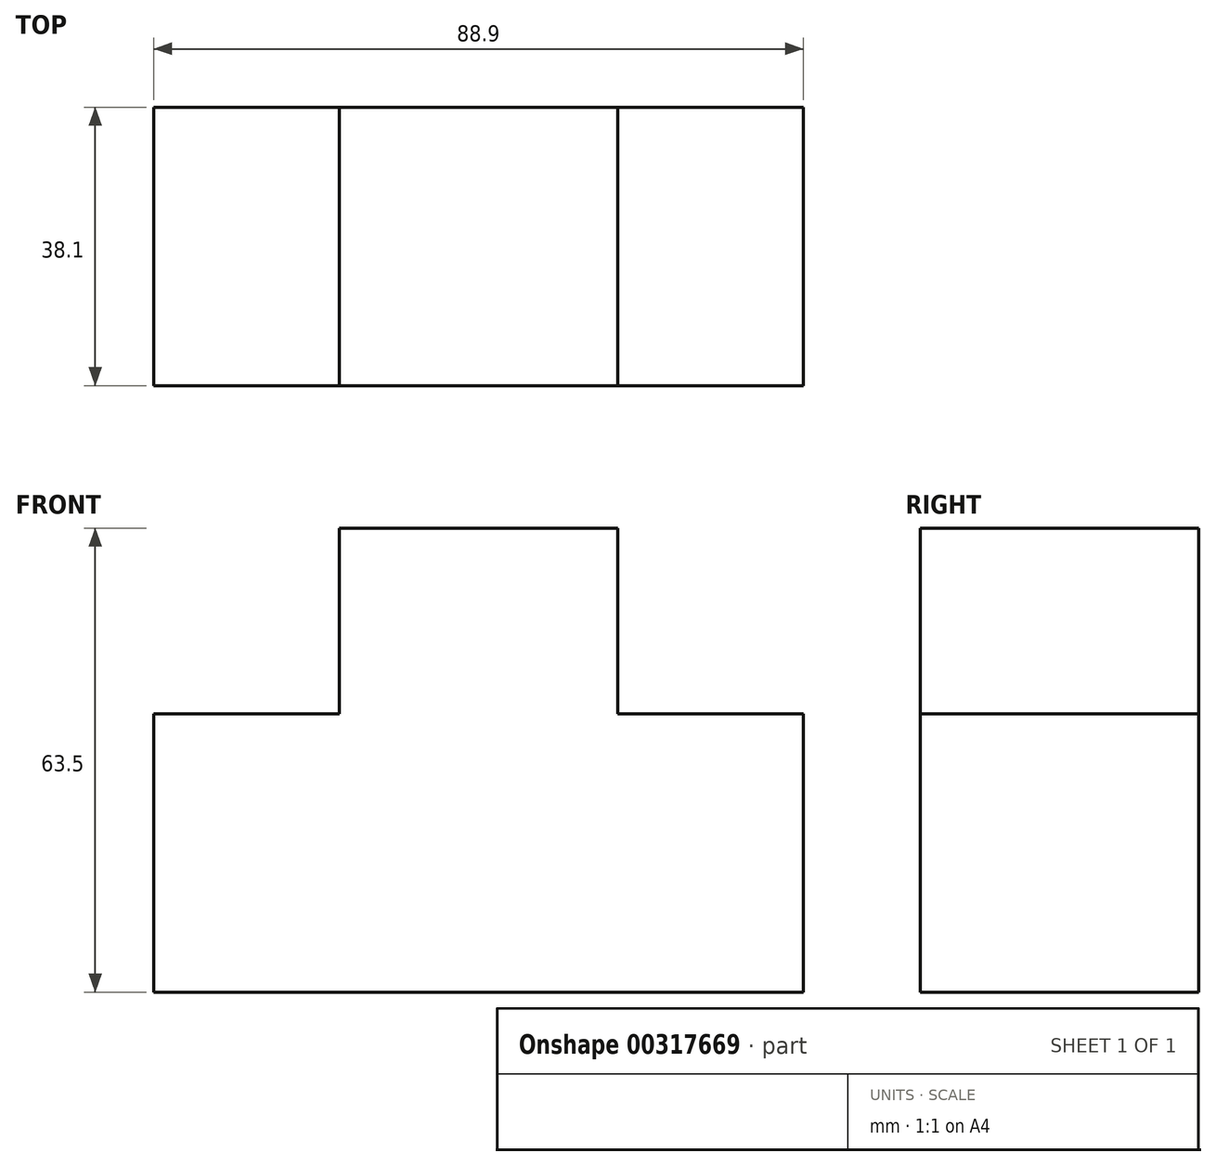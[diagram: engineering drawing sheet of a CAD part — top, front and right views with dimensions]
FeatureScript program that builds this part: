
annotation { "Feature Type Name" : "Feature", "Feature Type Description" : "" }
export const myFeature = defineFeature(function(context is Context, id is Id, definition is map)
    precondition{}
    {
        {
            var Q0;
            Q0=qCreatedBy(makeId("Front.planeOp"),FACE);
            var sketch = newSketch(context, id + "F0", { "sketchPlane" : qUnion([Q0])});
            skLineSegment(sketch, "E0", {"start": v(-63.5, 25.04) * mm, "end": v(-63.5, -13.06) * mm});
            skLineSegment(sketch, "E1", {"start": v(-63.5, -13.06) * mm, "end": v(25.4, -13.06) * mm});
            skLineSegment(sketch, "E2", {"start": v(25.4, -13.06) * mm, "end": v(25.4, 25.04) * mm});
            skLineSegment(sketch, "E3", {"start": v(25.4, 25.04) * mm, "end": v(0, 25.04) * mm});
            skLineSegment(sketch, "E4", {"start": v(-63.5, 25.04) * mm, "end": v(-38.1, 25.04) * mm});
            skLineSegment(sketch, "E5", {"start": v(-38.1, 25.04) * mm, "end": v(-38.1, 50.44) * mm});
            skLineSegment(sketch, "E6", {"start": v(-38.1, 50.44) * mm, "end": v(0, 50.44) * mm});
            skLineSegment(sketch, "E7", {"start": v(0, 50.44) * mm, "end": v(0, 25.04) * mm});
            skSolve(sketch);
        }
        {
            var Q0;
            Q0 = qSketchRegion(id + "F0", true);
            extrude(context, id + "F1", {"entities" : qUnion([Q0]), "depth" : 38.1 * mm});
        }
    });
